# Revit family: IS_Ceratherm100New_A4623_BIM_BE
name_source: partatom
category: Plumbing Fixtures
revit_build: Autodesk Revit 2015 (Build: 20140606_1530(x64)
units: mm (PartAtom-declared; Revit-internal decimal feet)

## types (1)
- A4623AA - Ceratherm 100 Mitigeur thermostatique bain/douche
    Accesoires = www.idealstandard.be
    Afwerking = Chroom
    Auteur = Ideal Standard Produktions-GmbH
    Barcode = 4015413320658
    Bedieningkraan = manueel met greep
    Bedieningkraanwerk = draaigreep
    Beschrijvinggarantie = Fabrieksgarantie
    BimObjectNaam = ISI_IdealStandard_Douche_Ceratherm_A4623AA
    Breedte = 0
    BrutoGewicht = 0
    Cost = 0 $
    Debiet = 21.5L/min | 3bar
    Default Elevation = 1219 mm
    Description = Ceratherm 100 Mitigeur thermostatique bain/douche
    Diepte = 0 mm  [stored 0 ft]
    Dimensions = 188 x 293 x 70 mm
    DuurEenheid = jaar
    Eigenschappen = CeraTherm 100 bad/douchethermostaat DN 15. perlator. Terugslagklep. Sprong 163 mm. Geluidsarme verdekte S-koppelingen (instelbaar van 137-163 mm).  Thermostatisch waspatroon. Temperatuurinstelling met extra temperatuurbegrenzing (kinderveiligheid). Bad/douche omstelling met keramische schijven (aan/uit functie en volumebegrenzer) ECO-stop (alleen voor douche).Geïntegreerde omsteller in volumeknop. Uithoudingstest EN 1111. Geluidsniveau volgens norm DIN 4109, Groep 1.
    Garantieonderdelen = 5
    Hauteur = 70 mm  [stored 0.229659 ft]
    IfcExportAs = IfcSanitaryTerminalType
    IfcExportType = Douche
    Installatieinstructies = www.idealstandard.be
    Kleur = Chroom
    Largeur = 293 mm
    Lengte = 0 mm  [stored 0 ft]
    Longueur = 188 mm
    Manufacturer = www.idealstandard.be
    Materiaal = messing verchroomd
    Merk = Ideal Standard
    Model = A4623AA
    Nettogewicht = 2.7
    Normen = EN 1111
DIN 4109
    Productinformatie = www.idealstandard.be
    Telefoonnummer = 0032 2 325 66 00
    Testdruk = 10 bar
    Typeconnectie = Sanitair
    Typekraanwerk = bad/douche
    URL = www.idealstandard.be
    Uniclass2015Beschrijving = Douche
    Uniclass2015Version = Products v1.1
    Urlproducent = www.idealstandard.be
    Versie = 1
    Vervangingskosten = 0
    Verwachtelevensduur = 25 jaar
    Volumeunits = liter
    Werkdruk = 1-5 bar

note: [stored X ft] marks values corroborated as IEEE doubles in the binary element streams (Revit-internal decimal feet)

## geometry (parser evidence)
native form markers: Blend x4, Sweep x1
no freeform markers — native parametric forms only
